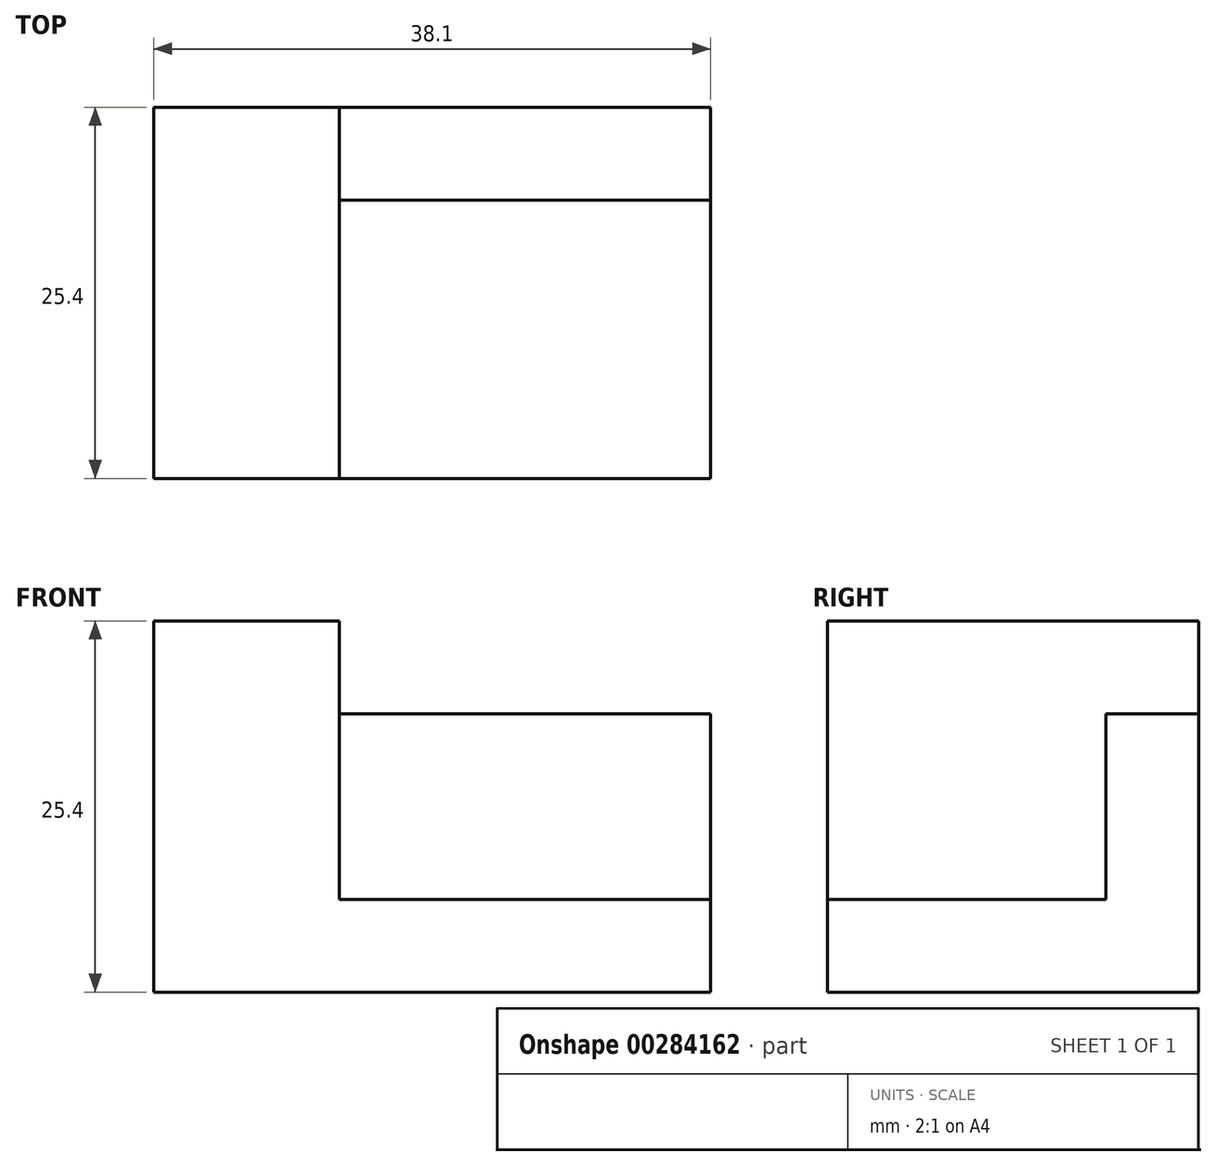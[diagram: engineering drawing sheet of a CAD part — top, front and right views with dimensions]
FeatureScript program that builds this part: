
annotation { "Feature Type Name" : "Feature", "Feature Type Description" : "" }
export const myFeature = defineFeature(function(context is Context, id is Id, definition is map)
    precondition{}
    {
        {
            var Q0;
            Q0=qCreatedBy(makeId("Front.planeOp"),FACE);
            var sketch = newSketch(context, id + "F0", { "sketchPlane" : qUnion([Q0])});
            skLineSegment(sketch, "E0.bottom", {"start": v(0, 0) * mm, "end": v(38.1, 0) * mm});
            skLineSegment(sketch, "E0.top", {"start": v(0, 25.4) * mm, "end": v(12.7, 25.4) * mm});
            skLineSegment(sketch, "E0.left", {"start": v(0, 0) * mm, "end": v(0, 25.4) * mm});
            skLineSegment(sketch, "E0.right", {"start": v(38.1, 0) * mm, "end": v(38.1, 6.35) * mm});
            skPoint(sketch, "E1", {"position": v(0, 25.4) * mm});
            skLineSegment(sketch, "E2", {"start": v(12.7, 25.4) * mm, "end": v(12.7, 6.35) * mm});
            skLineSegment(sketch, "E3", {"start": v(12.7, 6.35) * mm, "end": v(38.1, 6.35) * mm});
            skSolve(sketch);
        }
        {
            var Q0;
            Q0 = qSketchRegion(id + "F0", true);
            extrude(context, id + "F1", {"entities" : qUnion([Q0]), "depth" : 25.4 * mm});
        }
        {
            var Q0;
            Q0=makeQuery(id+"F1.opExtrude","SWEPT_FACE",FACE,{"disambiguationData":[OSD([sQuery(id+"F0.wireOp",EDGE,"E3")])]});
            var sketch = newSketch(context, id + "F2", { "sketchPlane" : qUnion([Q0])});
            skLineSegment(sketch, "E4.bottom", {"start": v(38.1, 0) * mm, "end": v(12.7, 0) * mm});
            skLineSegment(sketch, "E4.top", {"start": v(38.1, -6.35) * mm, "end": v(12.7, -6.35) * mm});
            skLineSegment(sketch, "E4.left", {"start": v(38.1, 0) * mm, "end": v(38.1, -6.35) * mm});
            skLineSegment(sketch, "E4.right", {"start": v(12.7, 0) * mm, "end": v(12.7, -6.35) * mm});
            skSolve(sketch);
        }
        {
            var Q0;
            Q0 = qSketchRegion(id + "F2", true);
            extrude(context, id + "F3", {"entities" : qUnion([Q0]), "operationType" : NewBodyOperationType.ADD, "depth" : 12.7 * mm});
        }
    });
